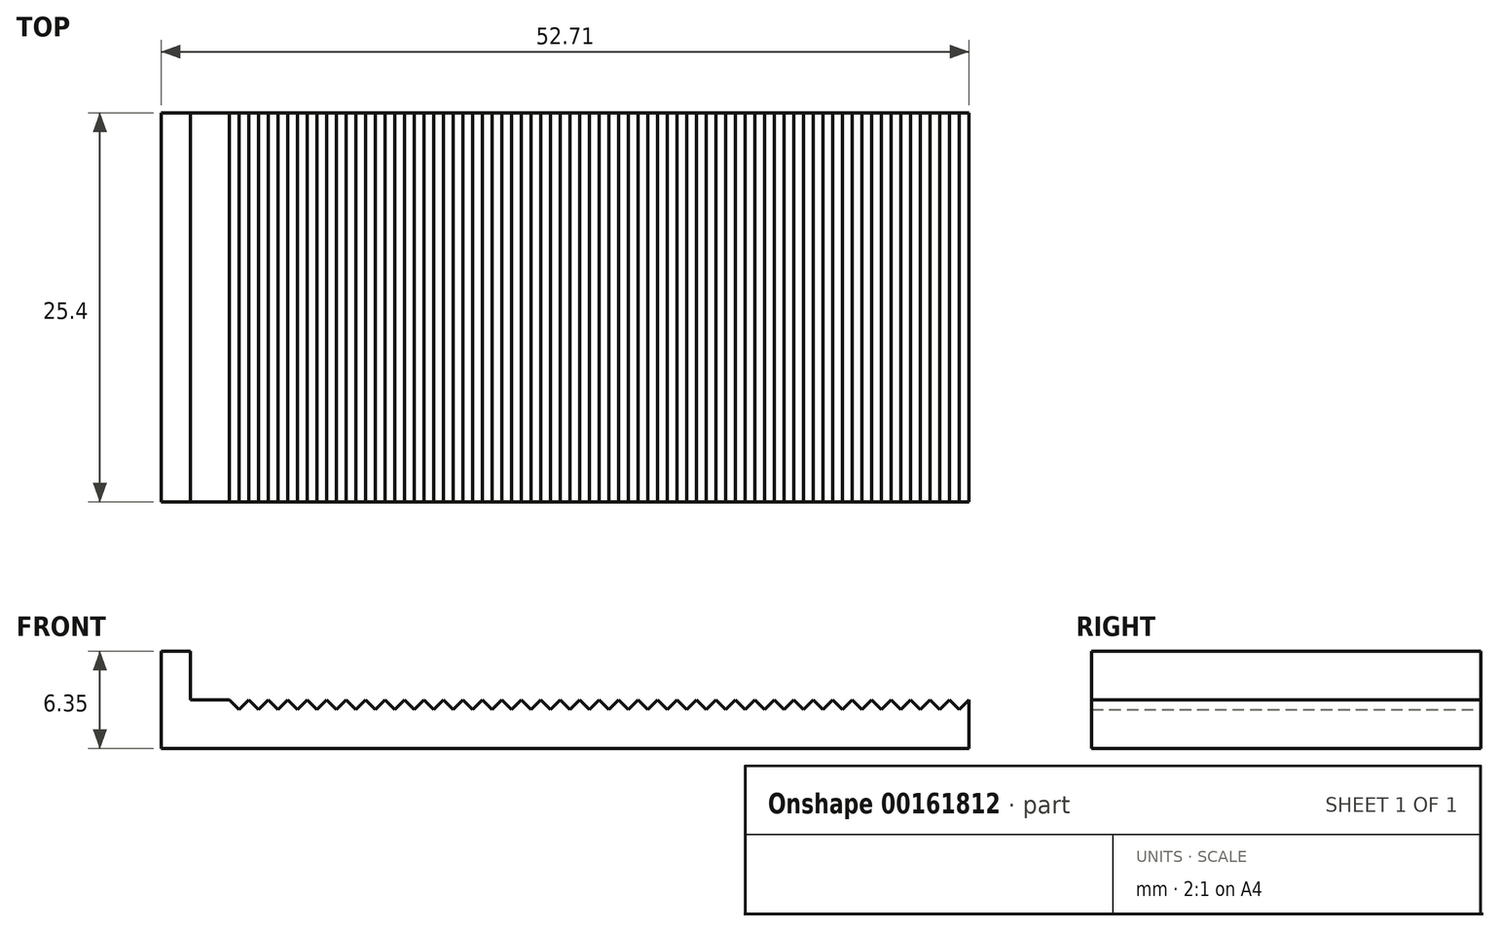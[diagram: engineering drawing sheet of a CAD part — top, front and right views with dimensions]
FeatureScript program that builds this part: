
annotation { "Feature Type Name" : "Feature", "Feature Type Description" : "" }
export const myFeature = defineFeature(function(context is Context, id is Id, definition is map)
    precondition{}
    {
        {
            var Q0;
            Q0=qCreatedBy(makeId("Front.planeOp"), FACE);
            var sketch = newSketch(context, id + "F0", { "sketchPlane" : qUnion([Q0])});
            skLineSegment(sketch, "E0", {"start": v(0, 0) * mm, "end": v(50.8, 0) * mm});
            skLineSegment(sketch, "E1", {"start": v(50.8, 0) * mm, "end": v(50.8, 3.17) * mm});
            skLineSegment(sketch, "E2", {"start": v(50.16, 2.54) * mm, "end": v(49.53, 3.18) * mm});
            skLineSegment(sketch, "E3", {"start": v(50.16, 2.54) * mm, "end": v(50.8, 3.18) * mm});
            skLineSegment(sketch, "E4.1.0.0", {"start": v(48.9, 2.54) * mm, "end": v(49.53, 3.18) * mm});
            skLineSegment(sketch, "E4.1.0.1", {"start": v(48.9, 2.54) * mm, "end": v(48.26, 3.18) * mm});
            skLineSegment(sketch, "E4.2.0.0", {"start": v(47.62, 2.54) * mm, "end": v(48.26, 3.18) * mm});
            skLineSegment(sketch, "E4.2.0.1", {"start": v(47.62, 2.54) * mm, "end": v(47, 3.18) * mm});
            skLineSegment(sketch, "E4.3.0.0", {"start": v(46.35, 2.54) * mm, "end": v(47, 3.18) * mm});
            skLineSegment(sketch, "E4.3.0.1", {"start": v(46.35, 2.54) * mm, "end": v(45.72, 3.18) * mm});
            skLineSegment(sketch, "E4.4.0.0", {"start": v(45.09, 2.54) * mm, "end": v(45.72, 3.18) * mm});
            skLineSegment(sketch, "E4.4.0.1", {"start": v(45.09, 2.54) * mm, "end": v(44.45, 3.18) * mm});
            skLineSegment(sketch, "E4.5.0.0", {"start": v(43.81, 2.54) * mm, "end": v(44.45, 3.18) * mm});
            skLineSegment(sketch, "E4.5.0.1", {"start": v(43.81, 2.54) * mm, "end": v(43.18, 3.18) * mm});
            skLineSegment(sketch, "E4.6.0.0", {"start": v(42.55, 2.54) * mm, "end": v(43.18, 3.18) * mm});
            skLineSegment(sketch, "E4.6.0.1", {"start": v(42.55, 2.54) * mm, "end": v(41.91, 3.18) * mm});
            skLineSegment(sketch, "E4.7.0.0", {"start": v(41.27, 2.54) * mm, "end": v(41.91, 3.18) * mm});
            skLineSegment(sketch, "E4.7.0.1", {"start": v(41.27, 2.54) * mm, "end": v(40.64, 3.18) * mm});
            skLineSegment(sketch, "E4.8.0.0", {"start": v(40, 2.54) * mm, "end": v(40.64, 3.18) * mm});
            skLineSegment(sketch, "E4.8.0.1", {"start": v(40, 2.54) * mm, "end": v(39.37, 3.18) * mm});
            skLineSegment(sketch, "E4.9.0.0", {"start": v(38.73, 2.54) * mm, "end": v(39.37, 3.18) * mm});
            skLineSegment(sketch, "E4.9.0.1", {"start": v(38.73, 2.54) * mm, "end": v(38.1, 3.18) * mm});
            skLineSegment(sketch, "E4.10.0.0", {"start": v(37.46, 2.54) * mm, "end": v(38.1, 3.18) * mm});
            skLineSegment(sketch, "E4.10.0.1", {"start": v(37.46, 2.54) * mm, "end": v(36.83, 3.18) * mm});
            skLineSegment(sketch, "E4.11.0.0", {"start": v(36.2, 2.54) * mm, "end": v(36.83, 3.18) * mm});
            skLineSegment(sketch, "E4.11.0.1", {"start": v(36.2, 2.54) * mm, "end": v(35.56, 3.18) * mm});
            skLineSegment(sketch, "E4.12.0.0", {"start": v(34.92, 2.54) * mm, "end": v(35.56, 3.18) * mm});
            skLineSegment(sketch, "E4.12.0.1", {"start": v(34.92, 2.54) * mm, "end": v(34.3, 3.18) * mm});
            skLineSegment(sketch, "E4.13.0.0", {"start": v(33.65, 2.54) * mm, "end": v(34.3, 3.18) * mm});
            skLineSegment(sketch, "E4.13.0.1", {"start": v(33.65, 2.54) * mm, "end": v(33.02, 3.18) * mm});
            skLineSegment(sketch, "E4.14.0.0", {"start": v(32.38, 2.54) * mm, "end": v(33.02, 3.18) * mm});
            skLineSegment(sketch, "E4.14.0.1", {"start": v(32.38, 2.54) * mm, "end": v(31.75, 3.18) * mm});
            skLineSegment(sketch, "E4.15.0.0", {"start": v(31.11, 2.54) * mm, "end": v(31.75, 3.18) * mm});
            skLineSegment(sketch, "E4.15.0.1", {"start": v(31.11, 2.54) * mm, "end": v(30.48, 3.18) * mm});
            skLineSegment(sketch, "E4.16.0.0", {"start": v(29.84, 2.54) * mm, "end": v(30.48, 3.18) * mm});
            skLineSegment(sketch, "E4.16.0.1", {"start": v(29.84, 2.54) * mm, "end": v(29.21, 3.18) * mm});
            skLineSegment(sketch, "E4.17.0.0", {"start": v(28.57, 2.54) * mm, "end": v(29.21, 3.18) * mm});
            skLineSegment(sketch, "E4.17.0.1", {"start": v(28.57, 2.54) * mm, "end": v(27.94, 3.18) * mm});
            skLineSegment(sketch, "E4.18.0.0", {"start": v(27.3, 2.54) * mm, "end": v(27.94, 3.18) * mm});
            skLineSegment(sketch, "E4.18.0.1", {"start": v(27.3, 2.54) * mm, "end": v(26.67, 3.18) * mm});
            skLineSegment(sketch, "E4.19.0.0", {"start": v(26.03, 2.54) * mm, "end": v(26.67, 3.18) * mm});
            skLineSegment(sketch, "E4.19.0.1", {"start": v(26.03, 2.54) * mm, "end": v(25.4, 3.18) * mm});
            skLineSegment(sketch, "E4.20.0.0", {"start": v(24.76, 2.54) * mm, "end": v(25.4, 3.18) * mm});
            skLineSegment(sketch, "E4.20.0.1", {"start": v(24.76, 2.54) * mm, "end": v(24.13, 3.18) * mm});
            skLineSegment(sketch, "E4.21.0.0", {"start": v(23.5, 2.54) * mm, "end": v(24.13, 3.18) * mm});
            skLineSegment(sketch, "E4.21.0.1", {"start": v(23.5, 2.54) * mm, "end": v(22.86, 3.18) * mm});
            skLineSegment(sketch, "E4.22.0.0", {"start": v(22.22, 2.54) * mm, "end": v(22.86, 3.18) * mm});
            skLineSegment(sketch, "E4.22.0.1", {"start": v(22.22, 2.54) * mm, "end": v(21.6, 3.18) * mm});
            skLineSegment(sketch, "E4.23.0.0", {"start": v(20.95, 2.54) * mm, "end": v(21.59, 3.18) * mm});
            skLineSegment(sketch, "E4.23.0.1", {"start": v(20.95, 2.54) * mm, "end": v(20.32, 3.18) * mm});
            skLineSegment(sketch, "E4.24.0.0", {"start": v(19.68, 2.54) * mm, "end": v(20.32, 3.18) * mm});
            skLineSegment(sketch, "E4.24.0.1", {"start": v(19.68, 2.54) * mm, "end": v(19.05, 3.18) * mm});
            skLineSegment(sketch, "E4.25.0.0", {"start": v(18.41, 2.54) * mm, "end": v(19.05, 3.18) * mm});
            skLineSegment(sketch, "E4.25.0.1", {"start": v(18.41, 2.54) * mm, "end": v(17.78, 3.18) * mm});
            skLineSegment(sketch, "E4.26.0.0", {"start": v(17.14, 2.54) * mm, "end": v(17.78, 3.18) * mm});
            skLineSegment(sketch, "E4.26.0.1", {"start": v(17.14, 2.54) * mm, "end": v(16.51, 3.18) * mm});
            skLineSegment(sketch, "E4.27.0.0", {"start": v(15.87, 2.54) * mm, "end": v(16.5, 3.18) * mm});
            skLineSegment(sketch, "E4.27.0.1", {"start": v(15.87, 2.54) * mm, "end": v(15.24, 3.18) * mm});
            skLineSegment(sketch, "E4.28.0.0", {"start": v(14.6, 2.54) * mm, "end": v(15.24, 3.18) * mm});
            skLineSegment(sketch, "E4.28.0.1", {"start": v(14.6, 2.54) * mm, "end": v(13.97, 3.18) * mm});
            skLineSegment(sketch, "E4.29.0.0", {"start": v(13.33, 2.54) * mm, "end": v(13.97, 3.18) * mm});
            skLineSegment(sketch, "E4.29.0.1", {"start": v(13.33, 2.54) * mm, "end": v(12.7, 3.18) * mm});
            skLineSegment(sketch, "E4.30.0.0", {"start": v(12.06, 2.54) * mm, "end": v(12.7, 3.18) * mm});
            skLineSegment(sketch, "E4.30.0.1", {"start": v(12.06, 2.54) * mm, "end": v(11.43, 3.18) * mm});
            skLineSegment(sketch, "E4.31.0.0", {"start": v(10.8, 2.54) * mm, "end": v(11.43, 3.18) * mm});
            skLineSegment(sketch, "E4.31.0.1", {"start": v(10.8, 2.54) * mm, "end": v(10.16, 3.18) * mm});
            skLineSegment(sketch, "E4.32.0.0", {"start": v(9.52, 2.54) * mm, "end": v(10.16, 3.18) * mm});
            skLineSegment(sketch, "E4.32.0.1", {"start": v(9.52, 2.54) * mm, "end": v(8.89, 3.18) * mm});
            skLineSegment(sketch, "E4.33.0.0", {"start": v(8.25, 2.54) * mm, "end": v(8.89, 3.18) * mm});
            skLineSegment(sketch, "E4.33.0.1", {"start": v(8.25, 2.54) * mm, "end": v(7.62, 3.18) * mm});
            skLineSegment(sketch, "E4.34.0.0", {"start": v(6.98, 2.54) * mm, "end": v(7.62, 3.18) * mm});
            skLineSegment(sketch, "E4.34.0.1", {"start": v(6.98, 2.54) * mm, "end": v(6.35, 3.18) * mm});
            skLineSegment(sketch, "E4.35.0.0", {"start": v(5.71, 2.54) * mm, "end": v(6.35, 3.18) * mm});
            skLineSegment(sketch, "E4.35.0.1", {"start": v(5.71, 2.54) * mm, "end": v(5.08, 3.18) * mm});
            skLineSegment(sketch, "E4.36.0.0", {"start": v(4.44, 2.54) * mm, "end": v(5.08, 3.18) * mm});
            skLineSegment(sketch, "E4.36.0.1", {"start": v(4.44, 2.54) * mm, "end": v(3.8, 3.18) * mm});
            skLineSegment(sketch, "E4.37.0.0", {"start": v(3.17, 2.54) * mm, "end": v(3.8, 3.18) * mm});
            skLineSegment(sketch, "E4.37.0.1", {"start": v(3.17, 2.54) * mm, "end": v(2.54, 3.18) * mm});
            skLineSegment(sketch, "E4.direction1", {"start": v(50.16, 2.54) * mm, "end": v(48.9, 2.54) * mm, "construction": true});
            skLineSegment(sketch, "E5.bottom", {"start": v(0, 0) * mm, "end": v(-1.9, 0) * mm});
            skLineSegment(sketch, "E5.top", {"start": v(0, 6.35) * mm, "end": v(-1.9, 6.35) * mm});
            skLineSegment(sketch, "E5.left", {"start": v(0, 3.17) * mm, "end": v(0, 6.35) * mm});
            skLineSegment(sketch, "E5.right", {"start": v(-1.9, 0) * mm, "end": v(-1.9, 6.35) * mm});
            skLineSegment(sketch, "E6", {"start": v(0, 3.17) * mm, "end": v(2.54, 3.17) * mm});
            skSolve(sketch);
        }
        {
            var Q0;
            Q0 = qSketchRegion(id + "F0", true);
            extrude(context, id + "F1", {"entities" : qUnion([Q0]), "depth" : 25.4 * mm, "offsetDistance" : 25.4 * mm});
        }
    });
